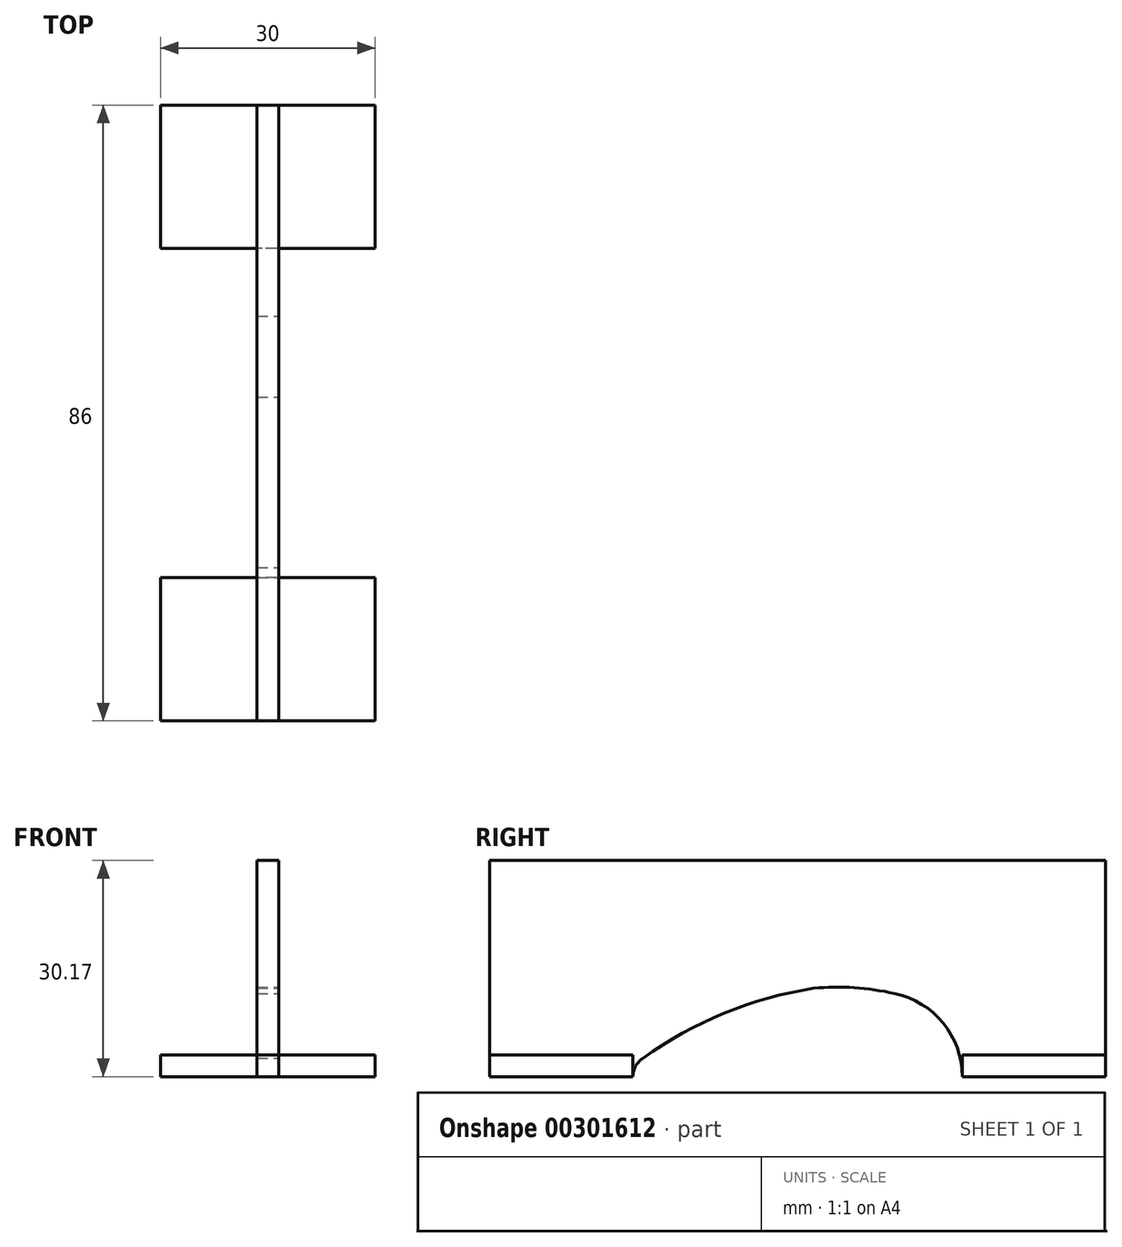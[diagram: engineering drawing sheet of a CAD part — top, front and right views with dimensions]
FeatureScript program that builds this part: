
annotation { "Feature Type Name" : "Feature", "Feature Type Description" : "" }
export const myFeature = defineFeature(function(context is Context, id is Id, definition is map)
    precondition{}
    {
        {
            var Q0;
            Q0=qCreatedBy(makeId("Top.planeOp"),FACE);
            var sketch = newSketch(context, id + "F0", { "sketchPlane" : qUnion([Q0])});
            skArc(sketch, "E0", {"start": v(0, -34.17) * mm, "mid": v(1.48, -33.79) * mm, "end": v(2.58, -32.72) * mm});
            skArc(sketch, "E1", {"start": v(2.58, -32.72) * mm, "mid": v(8.87, -21.4) * mm, "end": v(12.34, -8.91) * mm});
            skArc(sketch, "E2", {"start": v(12.34, -8.91) * mm, "mid": v(12.41, -3.24) * mm, "end": v(11.6, 2.37) * mm});
            skArc(sketch, "E3", {"start": v(11.6, 2.37) * mm, "mid": v(7.48, 9.17) * mm, "end": v(0, 11.83) * mm});
            skLineSegment(sketch, "E4.bottom", {"start": v(0, 31.83) * mm, "end": v(30.17, 31.83) * mm});
            skLineSegment(sketch, "E4.top", {"start": v(0, -54.17) * mm, "end": v(30.17, -54.17) * mm});
            skLineSegment(sketch, "E4.left", {"start": v(0, 31.83) * mm, "end": v(0, 11.83) * mm});
            skLineSegment(sketch, "E4.right", {"start": v(30.17, 31.83) * mm, "end": v(30.17, -54.17) * mm});
            skLineSegment(sketch, "E5.trimOffspring", {"start": v(0, -34.17) * mm, "end": v(0, -54.17) * mm});
            skSolve(sketch);
        }
        {
            var Q0;
            Q0=makeQuery(id+"F0.imprint","IMPRINT",FACE,{"disambiguationData":[TD([[makeQuery(id+"F0.imprint","IMPRINT",EDGE,{"derivedFrom":sQuery(id+"F0.wireOp",EDGE,"E0")}),-1.0]])]});
            extrude(context, id + "F1", {"entities" : qUnion([Q0]), "depth" : 3 * mm});
        }
        {
            var Q0;
            Q0=makeQuery(id+"F1.opExtrude","SWEPT_BODY",BODY,{"disambiguationData":[OSD([sQuery(id+"F0.wireOp",EDGE,"E0"),sQuery(id+"F0.wireOp",EDGE,"E1"),sQuery(id+"F0.wireOp",EDGE,"E2"),sQuery(id+"F0.wireOp",EDGE,"E3"),sQuery(id+"F0.wireOp",EDGE,"E4.bottom"),sQuery(id+"F0.wireOp",EDGE,"E4.top"),sQuery(id+"F0.wireOp",EDGE,"E4.left"),sQuery(id+"F0.wireOp",EDGE,"E4.right"),sQuery(id+"F0.wireOp",EDGE,"E5.trimOffspring")])]});
            var Q1;
            Q1=makeQuery(id+"F1.opExtrude","CAP_EDGE",EDGE,{"disambiguationData":[OSD([sQuery(id+"F0.wireOp",EDGE,"E5.trimOffspring")])],"isStart":false});
            transform(context, id + "F2", {"entities" : qUnion([Q0]), "transformType" : TransformType.ROTATION, "transformAxis" : qUnion([Q1]), "angle" : 90 * degree, "makeCopy" : false});
        }
        {
            var Q0;
            Q0=makeQuery(id+"F1.opExtrude","SWEPT_EDGE",EDGE,{"disambiguationData":[OSD([sQuery(id+"F0.wireOp",EDGE,"E4.top"),sQuery(id+"F0.wireOp",EDGE,"E5.trimOffspring")])]});
            cPoint(context, id + "F3", {"entities" : qUnion([Q0]), "parameter" : 0.5});
        }
        {
            var Q0;
            Q0=makeQuery(id+"F1.opExtrude","SWEPT_EDGE",EDGE,{"disambiguationData":[OSD([sQuery(id+"F0.wireOp",EDGE,"E4.top"),sQuery(id+"F0.wireOp",EDGE,"E4.right")])]});
            cPoint(context, id + "F4", {"entities" : qUnion([Q0]), "parameter" : 0.5});
        }
        {
            var Q0;
            Q0=makeQuery(id+"F1.opExtrude","SWEPT_EDGE",EDGE,{"disambiguationData":[OSD([sQuery(id+"F0.wireOp",EDGE,"E4.bottom"),sQuery(id+"F0.wireOp",EDGE,"E4.right")])]});
            cPoint(context, id + "F5", {"entities" : qUnion([Q0]), "parameter" : 0.5});
        }
        {
            var Q0;
            Q0 = qCreatedBy(id + "F3" ,VERTEX);
            var Q1;
            Q1 = qCreatedBy(id + "F4" ,VERTEX);
            var Q2;
            Q2 = qCreatedBy(id + "F5" ,VERTEX);
            cPlane(context, id + "F6", {"entities" : qUnion([Q0, Q1, Q2]), "cplaneType" : CPlaneType.THREE_POINT, "offset" : 25 * mm, "width" : 150 * mm, "height" : 150 * mm});
        }
        {
            var Q0;
            Q0=qCreatedBy(id+"F6.planeOp",FACE);
            var sketch = newSketch(context, id + "F7", { "sketchPlane" : qUnion([Q0])});
            skLineSegment(sketch, "E6.bottom", {"start": v(-54.17, 3) * mm, "end": v(-34.17, 3) * mm});
            skLineSegment(sketch, "E6.top", {"start": v(-54.17, 6) * mm, "end": v(-34.17, 6) * mm});
            skLineSegment(sketch, "E6.left", {"start": v(-54.17, 3) * mm, "end": v(-54.17, 6) * mm});
            skLineSegment(sketch, "E6.right", {"start": v(-34.17, 3) * mm, "end": v(-34.17, 6) * mm});
            skLineSegment(sketch, "E7.bottom", {"start": v(11.83, 3) * mm, "end": v(31.83, 3) * mm});
            skLineSegment(sketch, "E7.top", {"start": v(11.83, 6) * mm, "end": v(31.83, 6) * mm});
            skLineSegment(sketch, "E7.left", {"start": v(11.83, 3) * mm, "end": v(11.83, 6) * mm});
            skLineSegment(sketch, "E7.right", {"start": v(31.83, 3) * mm, "end": v(31.83, 6) * mm});
            skSolve(sketch);
        }
        {
            var Q0;
            Q0=makeQuery(id+"F7.imprint","IMPRINT",FACE,{"disambiguationData":[TD([[makeQuery(id+"F7.imprint","IMPRINT",EDGE,{"derivedFrom":sQuery(id+"F7.wireOp",EDGE,"E6.bottom")}),1.0]])]});
            var Q1;
            Q1=makeQuery(id+"F7.imprint","IMPRINT",FACE,{"disambiguationData":[TD([[makeQuery(id+"F7.imprint","IMPRINT",EDGE,{"derivedFrom":sQuery(id+"F7.wireOp",EDGE,"E7.bottom")}),1.0]])]});
            extrude(context, id + "F8", {"entities" : qUnion([Q0, Q1]), "endBound" : BoundingType.SYMMETRIC, "depth" : 30 * mm});
        }
    });
